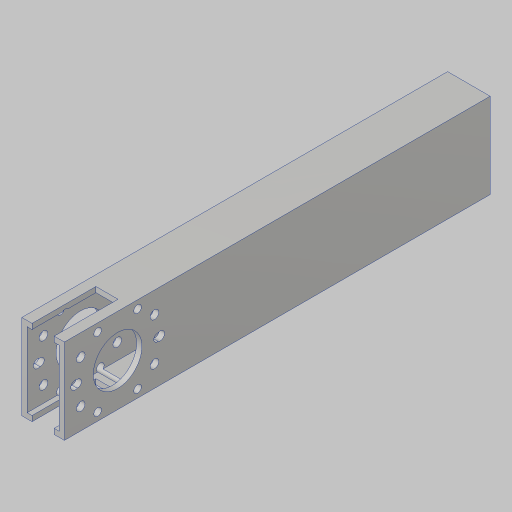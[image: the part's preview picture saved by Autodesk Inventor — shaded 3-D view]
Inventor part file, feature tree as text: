
AUTODESK INVENTOR PART (.ipt)
format: ipt  version: 2023.5 (Build 275446000, 446)  size: 175,616 bytes
history: native  units: in
note: dims shown in document units (in); Inventor stores cm internally (conversion verified against a paired STEP export)
features: hole x3, extrude x2, sketch x2, projected_geometry x1
ambient origin geometry x8: Origin, YZ Plane, XZ Plane, XY Plane, X Axis, Y Axis, Z Axis, Center Point
bodies: Solid1 (feature_tree)
feature tree (8):
  extrude  "Extrusion1"  Depth=1.25in
  sketch  "Sketch2"  dims[d4=0.0in d5=1.25in]
  hole  "Hole1"  [1 undecoded]
  hole  "Hole2"  [1 undecoded]
  hole  "Hole3"  [1 undecoded]
  extrude  "Extrusion2"  Depth=1.0in TaperAngle=360.0deg
  sketch  "Sketch3"  dims[d6=1.14in d7=0.75in d8=0.375in d9=0.25in d10=0.5635in d11=1.0in d12=0.8108in d13=1.875in d14=2.0in d15=4.7244in d17=360.0deg d19=2.3622in d21=360.0deg d23=0.201in d24=0.75in d25=0.332in d26=0.25in d27=0.5635in d28=1.0in d29=0.8108in d30=0.177in d31=0.75in d32=0.385in d33=0.25in d34=0.5635in d35=1.0in d36=0.8108in d37=0.52in d38=1.5in d39=1.0in d40=0.0in]
  projected_geometry  "Project Cut Edges1"
note: 3 required parameter values undecoded (feature->parameter linkage not recoverable at this tier; creation-order binding heuristic only, values carry confidence <= 0.55)
